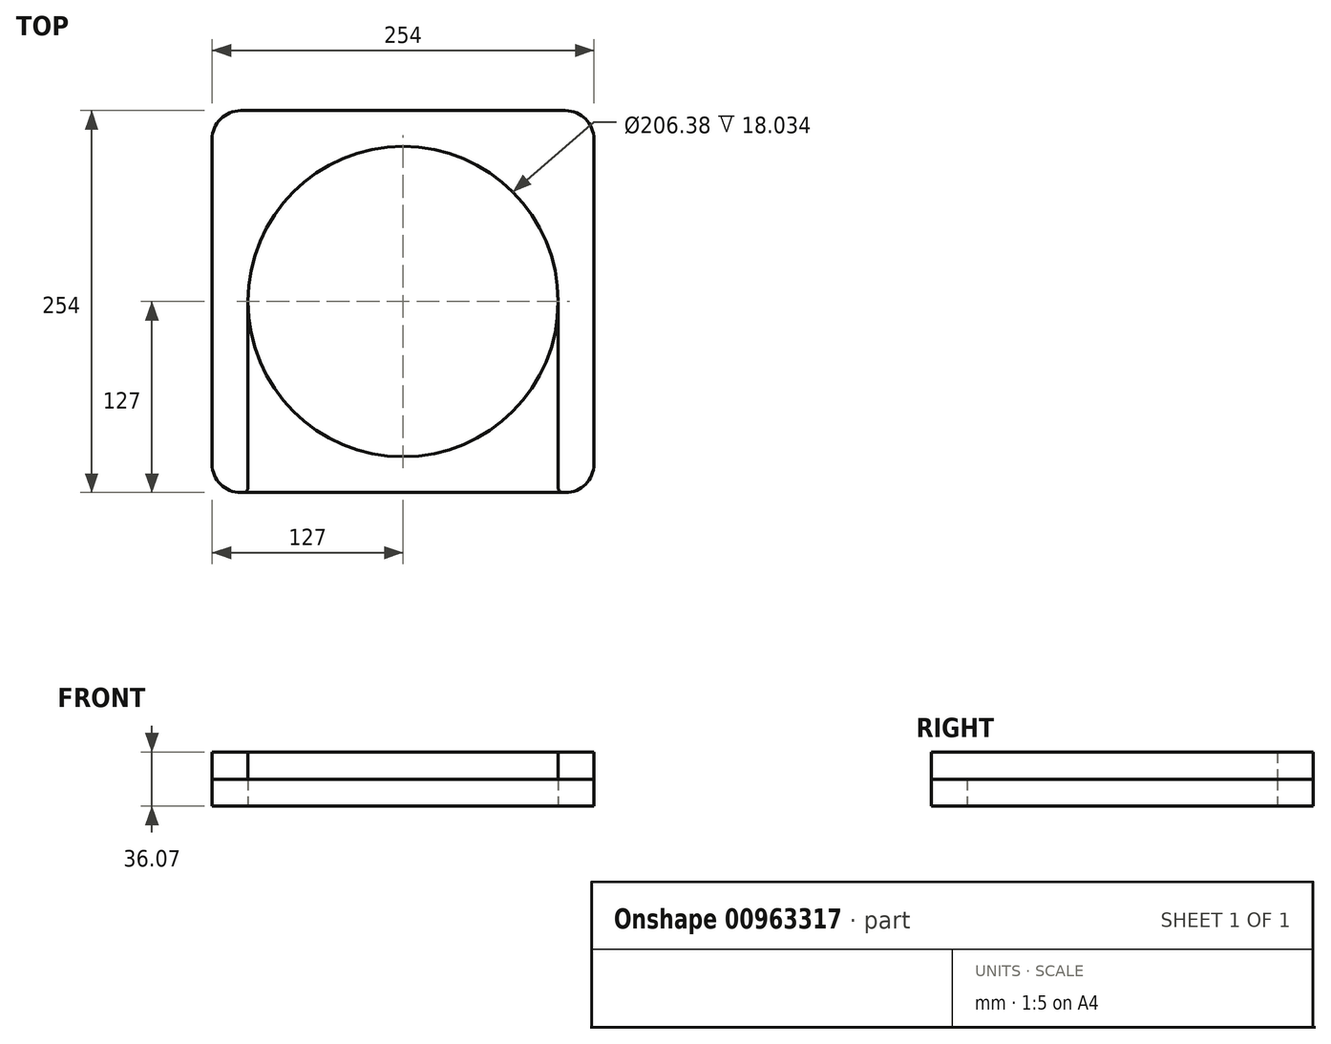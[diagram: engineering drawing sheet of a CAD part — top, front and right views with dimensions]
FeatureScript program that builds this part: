
annotation { "Feature Type Name" : "Feature", "Feature Type Description" : "" }
export const myFeature = defineFeature(function(context is Context, id is Id, definition is map)
    precondition{}
    {
        {
            var Q0;
            Q0=qCreatedBy(makeId("Top.planeOp"),FACE);
            var sketch = newSketch(context, id + "F0", { "sketchPlane" : qUnion([Q0])});
            skLineSegment(sketch, "E0.bottom", {"start": v(107.95, -127) * mm, "end": v(-107.95, -127) * mm});
            skLineSegment(sketch, "E0.top", {"start": v(107.95, 127) * mm, "end": v(-107.95, 127) * mm});
            skLineSegment(sketch, "E0.left", {"start": v(127, -107.95) * mm, "end": v(127, 107.95) * mm});
            skLineSegment(sketch, "E0.right", {"start": v(-127, -107.95) * mm, "end": v(-127, 107.95) * mm});
            skPoint(sketch, "E0.middle", {"position": v(0, 0) * mm});
            skCircle(sketch, "E1", {"center": v(0, 0) * mm, "radius": 103.19 * mm});
            skPoint(sketch, "E2.visualSharp", {"position": v(-127, 127) * mm});
            skArc(sketch, "E2.filletArc", {"start": v(-107.95, 127) * mm, "mid": v(-121.42, 121.42) * mm, "end": v(-127, 107.95) * mm});
            skPoint(sketch, "E3.visualSharp", {"position": v(-127, -127) * mm});
            skArc(sketch, "E3.filletArc", {"start": v(-127, -107.95) * mm, "mid": v(-121.42, -121.42) * mm, "end": v(-107.95, -127) * mm});
            skPoint(sketch, "E4.visualSharp", {"position": v(127, -127) * mm});
            skArc(sketch, "E4.filletArc", {"start": v(107.95, -127) * mm, "mid": v(121.42, -121.42) * mm, "end": v(127, -107.95) * mm});
            skPoint(sketch, "E5.visualSharp", {"position": v(127, 127) * mm});
            skArc(sketch, "E5.filletArc", {"start": v(127, 107.95) * mm, "mid": v(121.42, 121.42) * mm, "end": v(107.95, 127) * mm});
            skSolve(sketch);
        }
        {
            var Q0;
            Q0=makeQuery(id+"F0.imprint","IMPRINT",FACE,{"disambiguationData":[TD([[makeQuery(id+"F0.imprint","IMPRINT",EDGE,{"derivedFrom":sQuery(id+"F0.wireOp",EDGE,"E0.bottom")}),-1.0]])]});
            extrude(context, id + "F1", {"entities" : qUnion([Q0]), "depth" : 18.03 * mm, "offsetDistance" : 25.4 * mm});
        }
        {
            var Q0;
            Q0=makeQuery(id+"F1.opExtrude","CAP_FACE",FACE,{"disambiguationData":[OSD([sQuery(id+"F0.wireOp",EDGE,"E0.bottom"),sQuery(id+"F0.wireOp",EDGE,"E0.top"),sQuery(id+"F0.wireOp",EDGE,"E0.left"),sQuery(id+"F0.wireOp",EDGE,"E0.right"),sQuery(id+"F0.wireOp",EDGE,"E1"),sQuery(id+"F0.wireOp",EDGE,"E2.filletArc"),sQuery(id+"F0.wireOp",EDGE,"E3.filletArc"),sQuery(id+"F0.wireOp",EDGE,"E4.filletArc"),sQuery(id+"F0.wireOp",EDGE,"E5.filletArc")])],"isStart":false});
            var sketch = newSketch(context, id + "F2", { "sketchPlane" : qUnion([Q0])});
            skLineSegment(sketch, "E6", {"start": v(-103.19, 0) * mm, "end": v(-103.19, -127) * mm});
            skLineSegment(sketch, "E7", {"start": v(103.19, 0) * mm, "end": v(103.19, -127.04) * mm});
            skArc(sketch, "E8.0", {"start": v(103.19, 0) * mm, "mid": v(0, 103.19) * mm, "end": v(-103.19, 0) * mm});
            skLineSegment(sketch, "E9.0", {"start": v(-127, -107.95) * mm, "end": v(-127, 107.95) * mm});
            skArc(sketch, "E9.1", {"start": v(-127, -107.95) * mm, "mid": v(-121.42, -121.42) * mm, "end": v(-107.95, -127) * mm});
            skLineSegment(sketch, "E9.2", {"start": v(107.95, -127) * mm, "end": v(103.19, -127) * mm});
            skArc(sketch, "E9.3", {"start": v(107.95, -127) * mm, "mid": v(121.42, -121.42) * mm, "end": v(127, -107.95) * mm});
            skLineSegment(sketch, "E9.4", {"start": v(127, -107.95) * mm, "end": v(127, 107.95) * mm});
            skLineSegment(sketch, "E9.5", {"start": v(107.95, 127) * mm, "end": v(-107.95, 127) * mm});
            skArc(sketch, "E9.6", {"start": v(127, 107.95) * mm, "mid": v(121.42, 121.42) * mm, "end": v(107.95, 127) * mm});
            skArc(sketch, "E9.7", {"start": v(-107.95, 127) * mm, "mid": v(-121.42, 121.42) * mm, "end": v(-127, 107.95) * mm});
            skLineSegment(sketch, "E10.trimOffspring", {"start": v(-103.19, -127) * mm, "end": v(-107.95, -127) * mm});
            skSolve(sketch);
        }
        {
            var Q0;
            {var subQ1=sQuery(id+"F2.wireOp",EDGE,"E8.0");Q0=makeQuery(id+"F2.imprint","IMPRINT",FACE,{"disambiguationData":[TD([[makeQuery(id+"F2.imprint","IMPRINT",EDGE,{"derivedFrom":subQ1}),-1.0]])]});}
            extrude(context, id + "F3", {"entities" : qUnion([Q0]), "depth" : 18.03 * mm, "offsetDistance" : 25.4 * mm});
        }
        {
            var Q0;
            Q0=makeQuery(id+"F3.opExtrude","SWEPT_EDGE",EDGE,{"disambiguationData":[OSD([sQuery(id+"F0.wireOp",EDGE,"E0.bottom"),sQuery(id+"F2.wireOp",EDGE,"E6"),sQuery(id+"F2.wireOp",EDGE,"E10.trimOffspring")])]});
            var Q1;
            Q1=makeQuery(id+"F3.opExtrude","SWEPT_EDGE",EDGE,{"disambiguationData":[OSD([sQuery(id+"F0.wireOp",EDGE,"E0.bottom"),sQuery(id+"F2.wireOp",EDGE,"E7"),sQuery(id+"F2.wireOp",EDGE,"E9.2")])]});
            fillet(context, id + "F4", {"entities" : qUnion([Q0, Q1]), "radius" : 3.17 * mm, "tangentPropagation" : true, "allowEdgeOverflow" : false});
        }
    });
